# Revit family: QF_ELECTROLUXPROFESSIONAL_586277_PUET17KUEO
name_source: partatom
category: Specialty Equipment
revit_build: Autodesk Revit 2018 (Build: 20190510_1515(x64)
units: mm (PartAtom-declared; Revit-internal decimal feet)

## family parameters
Always vertical = Yes
Cut with Voids When Loaded = No
Part Type = Normal
Room Calculation Point = No
Round Connector Dimension = Use Radius
Shared = Yes
Work Plane-Based = No

## types (1)
- 586277_EL. TILTING PRESS. BRAIS. PAN+STEAM+CTS_170L_WALL MOUNTED
    50 Hertz Option = No
    60 Hertz Option = Yes
    Apparent Power = 0 VA
    Base Height = 500 mm  [stored 1.64042 ft]
    Code = 0
    Cold Water Connection Height = 395 mm  [stored 1.29593 ft]
    Cold Water Radius Size = 6.35 mm  [stored 0.0208333 ft]
    Cold Water Size = 1"
    Conn Conduit = Yes
    Cycle = 60 Hz
    Depth = 850 mm  [stored 2.78871 ft]
    Description = High Productivity Cooking Electric Tilting Pressure Braising Pan-170lt- Wall Mounted with CTS
    Direct Waste Size = 1"
    Elec Conn Connection Height = 450 mm  [stored 1.47638 ft]
    Electrical Remarks = 3PH+N 50/60HZ COMPATIBLE
    FL Amps = 0 A
    HP = 27.6 HP
    Height = 900 mm  [stored 2.95276 ft]
    Hot Water Connection Height = 395 mm  [stored 1.29593 ft]
    Hot Water Flow = 0 GPM
    Hot Water Radius Size = 6.35 mm  [stored 0.0208333 ft]
    Hot Water Size = 1"
    Indirect Waste Connection Height = 0 mm  [stored 0 ft]
    Indirect Waste Radius Size = 12.7 mm  [stored 0.0416667 ft]
    Indirect Waste Size = 1"
    Manufacturer = ELECTROLUX
    Max Overcurrent Protection = 5 A
    Min Ckt Ampacity = 0 A
    Model = 586277
    Phase = 3
    Plumbing Remarks = For Domestic Water Connection
    URL = www.electrolux.com/foodservice
    URL Cutsheet = www.electrolux.com/foodservice
    URL Manufacturer = www.electrolux.com/foodservice
    Volts = 400 V
    Watts = 0 W
    Weight = 340 kg
    Width = 1600 mm  [stored 5.24934 ft]

note: [stored X ft] marks values corroborated as IEEE doubles in the binary element streams (Revit-internal decimal feet)

## geometry (parser evidence)
native form markers: Blend x27, Sweep x2
no freeform markers — native parametric forms only
